# Revit family: YGNIS_Recuperador humos Totaleco Simple
name_source: partatom
category: Equipos mecánicos
revit_build: Autodesk Revit 2016 (Build: 20150220_1215(x64)
units: mm (PartAtom-declared; Revit-internal decimal feet)

## family parameters
Compartido = No
Corte con vacíos al cargar = No
Cota de conector redondo = Diámetro de uso
Número OmniClass = 23.75.00.00
Punto de cálculo de habitación = No
Se basa en plano de trabajo = No
Siempre vertical = Sí
Tipo de pieza = Normal
Título OmniClass = Climate Control (HVAC)

## types (12) — shared parameters
ACS Biplano = Sí
ACS Uniplano = No
Altura patas = 58 mm
Asas = 300 mm
Código de montaje = D3090
Descripción = Recuperador de humos con extractor incorporado de 400 a 1430 KW
Fabricante = YGNIS Atlantic
Material = Acero
Material tomas = Acero azul
Modelo = Totaleco 3T Bi
ø toma de vaciado = 12.7 mm  [stored 0.0416667 ft]

## per-type parameters (varying)
- T3: A, anchura=1245 mm; Agua T1 - T14=Sí; Agua T18 - T56=No; B, altura=1175 mm; C, profundidad=538 mm; Caudal mínimo=6 m³/h; D=970 mm; D empalmes=125 mm  [stored 0.410105 ft]; E entrada humos=300 mm; E.2=295 mm; F=270 mm; G salida humos=250 mm  [stored 0.82021 ft]; G.2=245 mm  [stored 0.803806 ft]; H=493 mm; I=224 mm  [stored 0.734908 ft]; J=448 mm; K=1096 mm; L=138 mm  [stored 0.452756 ft]; M=259 mm; N=200 mm  [stored 0.656168 ft]; N.2=195 mm  [stored 0.639764 ft]; O=326 mm; P=70 mm  [stored 0.229659 ft]; Q=119 mm  [stored 0.39042 ft]; R hueco entrada humos=157.5 mm  [stored 0.516732 ft]; ø condensados=32 mm  [stored 0.104987 ft]; ø impulsión/retorno=65 mm  [stored 0.213255 ft]; ø válvula de seguridad=12.7 mm  [stored 0.0416667 ft]
- T1: A, anchura=770 mm; Agua T1 - T14=Sí; Agua T18 - T56=No; B, altura=995 mm; C, profundidad=538 mm; Caudal mínimo=3 m³/h; D=840 mm; D empalmes=125 mm  [stored 0.410105 ft]; E entrada humos=200 mm  [stored 0.656168 ft]; E.2=195 mm  [stored 0.639764 ft]; F=215 mm; G salida humos=200 mm  [stored 0.656168 ft]; G.2=195 mm  [stored 0.639764 ft]; H=413 mm; I=224 mm  [stored 0.734908 ft]; J=448 mm; K=621 mm; L=108 mm  [stored 0.354331 ft]; M=203 mm  [stored 0.66601 ft]; N=180 mm  [stored 0.590551 ft]; N.2=175 mm  [stored 0.574147 ft]; O=326 mm; P=70 mm  [stored 0.229659 ft]; Q=119 mm  [stored 0.39042 ft]; R hueco entrada humos=107.5 mm; ø condensados=32 mm  [stored 0.104987 ft]; ø impulsión/retorno=65 mm  [stored 0.213255 ft]; ø válvula de seguridad=12.7 mm  [stored 0.0416667 ft]
- T2: A, anchura=965 mm; Agua T1 - T14=Sí; Agua T18 - T56=No; B, altura=1080 mm; C, profundidad=538 mm; Caudal mínimo=4 m³/h; D=900 mm; D empalmes=125 mm  [stored 0.410105 ft]; E entrada humos=250 mm  [stored 0.82021 ft]; E.2=245 mm  [stored 0.803806 ft]; F=250 mm  [stored 0.82021 ft]; G salida humos=200 mm  [stored 0.656168 ft]; G.2=195 mm  [stored 0.639764 ft]; H=448 mm; I=224 mm  [stored 0.734908 ft]; J=448 mm; K=816 mm; L=123 mm  [stored 0.403543 ft]; M=228 mm  [stored 0.748031 ft]; N=180 mm  [stored 0.590551 ft]; N.2=175 mm  [stored 0.574147 ft]; O=326 mm; P=70 mm  [stored 0.229659 ft]; Q=119 mm  [stored 0.39042 ft]; R hueco entrada humos=132.5 mm; ø condensados=32 mm  [stored 0.104987 ft]; ø impulsión/retorno=65 mm  [stored 0.213255 ft]; ø válvula de seguridad=12.7 mm  [stored 0.0416667 ft]
- T4: A, anchura=989 mm; Agua T1 - T14=Sí; Agua T18 - T56=No; B, altura=1400 mm; C, profundidad=538 mm; Caudal mínimo=8 m³/h; D=1170 mm; D empalmes=125 mm  [stored 0.410105 ft]; E entrada humos=350 mm; E.2=345 mm; F=300 mm; G salida humos=300 mm; G.2=295 mm; H=567 mm; I=306 mm; J=448 mm; K=840 mm; L=143 mm; M=292 mm; N=250 mm  [stored 0.82021 ft]; N.2=245 mm  [stored 0.803806 ft]; O=326 mm; P=70 mm  [stored 0.229659 ft]; Q=119 mm  [stored 0.39042 ft]; R hueco entrada humos=182.5 mm  [stored 0.598753 ft]; ø condensados=32 mm  [stored 0.104987 ft]; ø impulsión/retorno=65 mm  [stored 0.213255 ft]; ø válvula de seguridad=12.7 mm  [stored 0.0416667 ft]
- T10: A, anchura=1427 mm; Agua T1 - T14=Sí; Agua T18 - T56=No; B, altura=1650 mm; C, profundidad=650 mm; Caudal mínimo=19 m³/h; D=1345 mm; D empalmes=125 mm  [stored 0.410105 ft]; E entrada humos=500 mm; E.2=495 mm; F=350 mm; G salida humos=400 mm; G.2=395 mm; H=680 mm; I=280 mm; J=560 mm; K=1278 mm; L=143 mm; M=343 mm; N=350 mm; N.2=345 mm; O=326 mm; P=70 mm  [stored 0.229659 ft]; Q=119 mm  [stored 0.39042 ft]; R hueco entrada humos=257.5 mm; ø condensados=32 mm  [stored 0.104987 ft]; ø impulsión/retorno=65 mm  [stored 0.213255 ft]; ø válvula de seguridad=12.7 mm  [stored 0.0416667 ft]
- T14: A, anchura=1577 mm; Agua T1 - T14=Sí; Agua T18 - T56=No; B, altura=1850 mm; C, profundidad=706 mm; Caudal mínimo=25 m³/h; D=1345 mm; D empalmes=125 mm  [stored 0.410105 ft]; E entrada humos=500 mm; E.2=495 mm; F=350 mm; G salida humos=400 mm; G.2=395 mm; H=680 mm; I=280 mm; J=616 mm; K=1428 mm; L=143 mm; M=337 mm; N=350 mm; N.2=345 mm; O=326 mm; P=70 mm  [stored 0.229659 ft]; Q=119 mm  [stored 0.39042 ft]; R hueco entrada humos=257.5 mm; ø condensados=32 mm  [stored 0.104987 ft]; ø impulsión/retorno=65 mm  [stored 0.213255 ft]; ø válvula de seguridad=12.7 mm  [stored 0.0416667 ft]
- T7: A, anchura=1310 mm; Agua T1 - T14=Sí; Agua T18 - T56=No; B, altura=1505 mm; C, profundidad=538 mm; Caudal mínimo=12 m³/h; D=1250 mm; D empalmes=125 mm  [stored 0.410105 ft]; E entrada humos=400 mm; E.2=395 mm; F=330 mm; G salida humos=350 mm; G.2=345 mm; H=622 mm; I=306 mm; J=448 mm; K=1161 mm; L=146 mm  [stored 0.479003 ft]; M=340 mm; N=250 mm  [stored 0.82021 ft]; N.2=245 mm  [stored 0.803806 ft]; O=326 mm; P=70 mm  [stored 0.229659 ft]; Q=119 mm  [stored 0.39042 ft]; R hueco entrada humos=207.5 mm  [stored 0.680774 ft]; ø condensados=32 mm  [stored 0.104987 ft]; ø impulsión/retorno=65 mm  [stored 0.213255 ft]; ø válvula de seguridad=12.7 mm  [stored 0.0416667 ft]
- T18: A, anchura=1795 mm; Agua T1 - T14=No; Agua T18 - T56=Sí; B, altura=1790 mm; C, profundidad=712 mm; Caudal mínimo=33 m³/h; D=1450 mm; D empalmes=210 mm  [stored 0.688976 ft]; E entrada humos=550 mm; E.2=545 mm; F=415 mm; G salida humos=450 mm; G.2=445 mm; H=784 mm; I=252 mm  [stored 0.826772 ft]; J=672 mm; K=1602 mm; L=162 mm  [stored 0.531496 ft]; M=382 mm; N=400 mm; N.2=395 mm; O=205 mm  [stored 0.672572 ft]; P=80 mm  [stored 0.262467 ft]; Q=163 mm  [stored 0.534777 ft]; R hueco entrada humos=282.5 mm; ø condensados=32 mm  [stored 0.104987 ft]; ø impulsión/retorno=150 mm; ø válvula de seguridad=25.4 mm  [stored 0.0833333 ft]
- T24: A, anchura=2080 mm; Agua T1 - T14=No; Agua T18 - T56=Sí; B, altura=2140 mm; C, profundidad=820 mm; Caudal mínimo=42 m³/h; D=1695 mm; D empalmes=260 mm; E entrada humos=650 mm; E.2=645 mm; F=535 mm; G salida humos=550 mm; G.2=545 mm; H=945 mm; I=279 mm; J=728 mm; K=1824 mm; L=228 mm  [stored 0.748031 ft]; M=506 mm; N=500 mm; N.2=495 mm; O=340 mm; P=120 mm  [stored 0.393701 ft]; Q=226 mm  [stored 0.74147 ft]; R hueco entrada humos=332.5 mm; ø condensados=63 mm  [stored 0.206693 ft]; ø impulsión/retorno=200 mm  [stored 0.656168 ft]; ø válvula de seguridad=25.4 mm  [stored 0.0833333 ft]
- T32: A, anchura=2290 mm; Agua T1 - T14=No; Agua T18 - T56=Sí; B, altura=2370 mm; C, profundidad=931 mm; Caudal mínimo=56 m³/h; D=1875 mm; D empalmes=260 mm; E entrada humos=750 mm; E.2=745 mm; F=615 mm; G salida humos=650 mm; G.2=645 mm; H=1075 mm; I=279 mm; J=840 mm; K=2034 mm; L=220 mm  [stored 0.721785 ft]; M=553 mm; N=600 mm; N.2=595 mm; O=374 mm; P=120 mm  [stored 0.393701 ft]; Q=226 mm  [stored 0.74147 ft]; R hueco entrada humos=382.5 mm; ø condensados=63 mm  [stored 0.206693 ft]; ø impulsión/retorno=200 mm  [stored 0.656168 ft]; ø válvula de seguridad=25.4 mm  [stored 0.0833333 ft]
- T42: A, anchura=2500 mm; Agua T1 - T14=No; Agua T18 - T56=Sí; B, altura=2570 mm; C, profundidad=1043 mm; Caudal mínimo=74 m³/h; D=2025 mm; D empalmes=260 mm; E entrada humos=850 mm; E.2=845 mm; F=690 mm; G salida humos=700 mm; G.2=695 mm; H=1175 mm; I=279 mm; J=952 mm; K=2244 mm; L=245 mm  [stored 0.803806 ft]; M=611 mm; N=700 mm; N.2=695 mm; O=424 mm; P=120 mm  [stored 0.393701 ft]; Q=226 mm  [stored 0.74147 ft]; R hueco entrada humos=432.5 mm; ø condensados=63 mm  [stored 0.206693 ft]; ø impulsión/retorno=200 mm  [stored 0.656168 ft]; ø válvula de seguridad=31.75 mm
- T56: A, anchura=2530 mm; Agua T1 - T14=No; Agua T18 - T56=Sí; B, altura=2740 mm; C, profundidad=1267 mm; Caudal mínimo=97 m³/h; D=2145 mm; D empalmes=260 mm; E entrada humos=950 mm; E.2=945 mm; F=705 mm; G salida humos=800 mm; G.2=795 mm; H=1245 mm; I=279 mm; J=1176 mm; K=2274 mm; L=245 mm  [stored 0.803806 ft]; M=682 mm; N=800 mm; N.2=795 mm; O=648 mm; P=120 mm  [stored 0.393701 ft]; Q=226 mm  [stored 0.74147 ft]; R hueco entrada humos=482.5 mm; ø condensados=63 mm  [stored 0.206693 ft]; ø impulsión/retorno=200 mm  [stored 0.656168 ft]; ø válvula de seguridad=31.75 mm

note: [stored X ft] marks values corroborated as IEEE doubles in the binary element streams (Revit-internal decimal feet)
